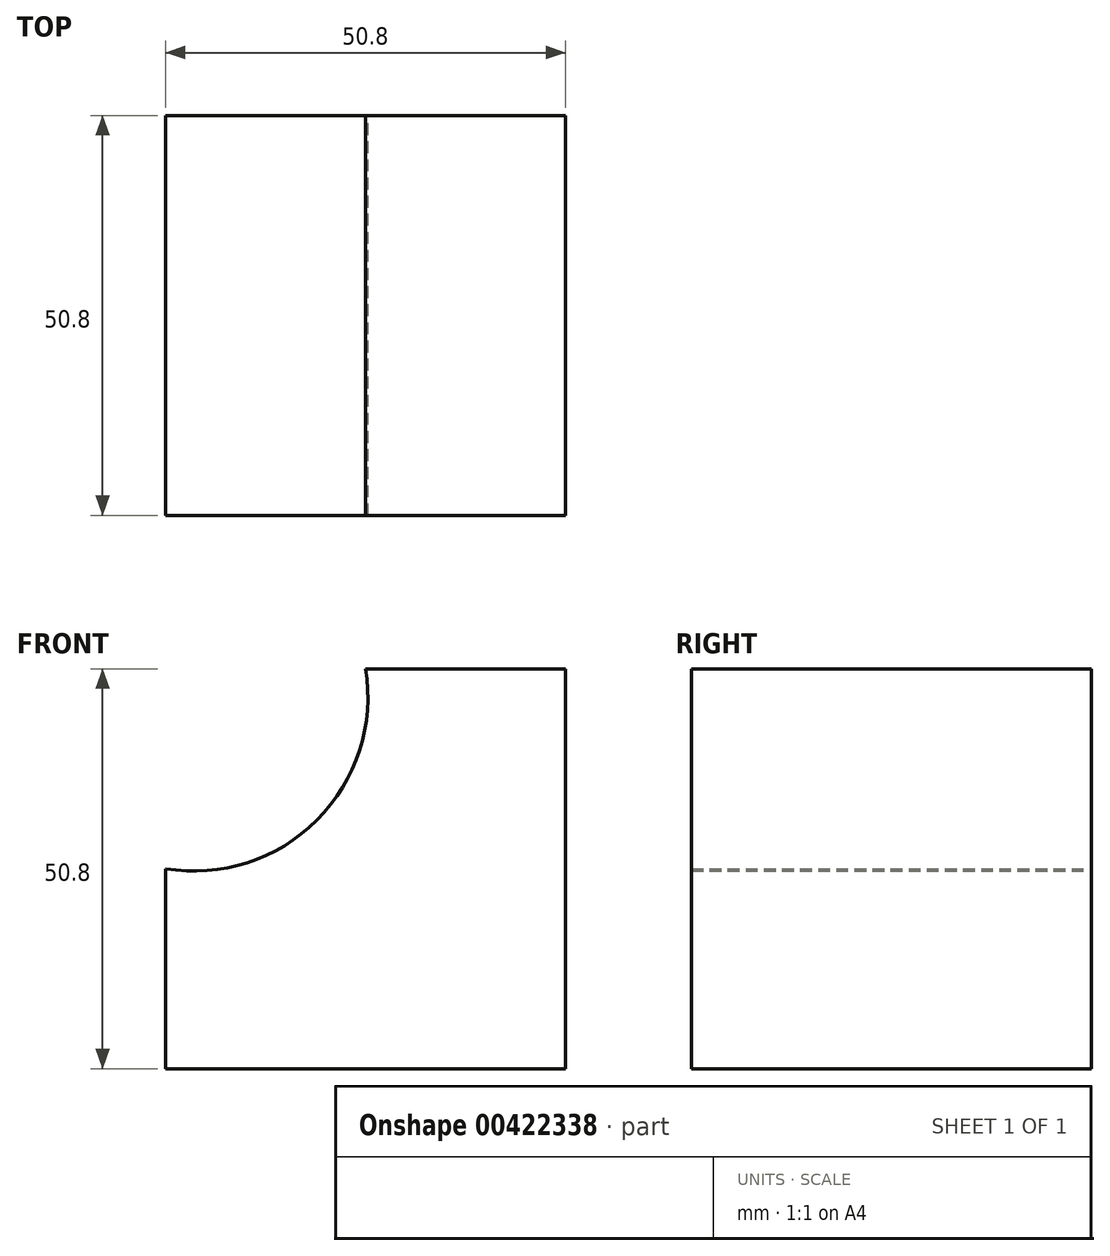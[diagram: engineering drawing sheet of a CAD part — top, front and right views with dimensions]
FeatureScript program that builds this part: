
annotation { "Feature Type Name" : "Feature", "Feature Type Description" : "" }
export const myFeature = defineFeature(function(context is Context, id is Id, definition is map)
    precondition{}
    {
        {
            var Q0;
            Q0=qCreatedBy(makeId("Front.planeOp"),FACE);
            var sketch = newSketch(context, id + "F0", { "sketchPlane" : qUnion([Q0])});
            skLineSegment(sketch, "E0", {"start": v(0, 0) * mm, "end": v(-50.8, 0) * mm});
            skLineSegment(sketch, "E1", {"start": v(0, 0) * mm, "end": v(0, 50.8) * mm});
            skLineSegment(sketch, "E2", {"start": v(0, 50.8) * mm, "end": v(-25.4, 50.8) * mm});
            skLineSegment(sketch, "E3", {"start": v(-50.8, 0) * mm, "end": v(-50.8, 25.4) * mm});
            skArc(sketch, "E4", {"start": v(-50.8, 25.4) * mm, "mid": v(-31.58, 31.58) * mm, "end": v(-25.4, 50.8) * mm});
            skSolve(sketch);
        }
        {
            var Q0;
            Q0 = qSketchRegion(id + "F0", true);
            extrude(context, id + "F1", {"entities" : qUnion([Q0]), "depth" : 50.8 * mm});
        }
    });
